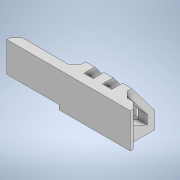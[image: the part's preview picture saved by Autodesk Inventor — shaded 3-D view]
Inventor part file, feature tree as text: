
AUTODESK INVENTOR PART (.ipt)
format: ipt  version: 2020.1 (Build 241239000, 239)  size: 230,400 bytes
history: native  units: mm
features: extrude x7, sketch x7, chamfer x2
ambient origin geometry x8: Origin, YZ Plane, XZ Plane, XY Plane, X Axis, Y Axis, Z Axis, Center Point
bodies: Solid1 (feature_tree)
feature tree (16):
  extrude  "Extrusion1"  Depth=14.0mm
  extrude  "Extrusion2"  Depth=5.0mm
  extrude  "Extrusion3"  Depth=10.0mm
  extrude  "Extrusion5"  Depth=1.0mm
  chamfer  "Chamfer1"  Distance=3.0mm
  chamfer  "Chamfer2"  Distance=2.0mm
  extrude  "Extrusion6"  Depth=2.0mm
  extrude  "Extrusion7"  Depth=2.0mm
  extrude  "Extrusion8"  Depth=1.5mm TaperAngle=0.0deg
  sketch  "Sketch1"  dims[d0=5.0mm d1=14.0mm]
  sketch  "Sketch2"  dims[d2=14.0mm d3=5.0mm]
  sketch  "Sketch3"  dims[d4=10.0mm d5=10.0mm]
  sketch  "Sketch4"  dims[d6=10.0mm d9=1.0mm]
  sketch  "Sketch5"  dims[d10=1.0mm]
  sketch  "Sketch6"  dims[d11=1.0mm d12=3.0mm d13=0.0mm]
  sketch  "Sketch7"  dims[d16=12.0mm d17=2.0mm d19=2.0mm d20=2.0mm d21=16.0mm d22=0.0mm d27=3.0mm d28=3.0mm d29=3.0mm d30=3.0mm d31=3.0mm d32=15.0mm d33=0.0mm d34=2.0mm d35=1.5mm d37=2.0mm d38=1.0mm d41=25.0mm d42=0.0mm d43=2.0mm d44=2.0mm d45=45.0deg d46=2.0mm d47=2.0mm d48=45.0deg d49=1.1mm d50=7.0mm d51=15.0mm d52=0.0mm d53=1.5mm d54=10.0mm d55=0.0mm d56=0.7mm d57=10.0mm d58=0.0mm d39=0.5mm d40=0.872665mm]
